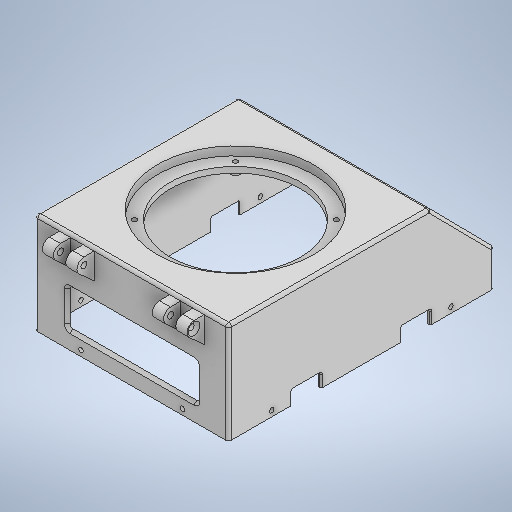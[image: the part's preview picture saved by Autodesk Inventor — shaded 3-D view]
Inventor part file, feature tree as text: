
AUTODESK INVENTOR PART (.ipt)
format: ipt  version: 2025.1 (Build 291241000, 241)  size: 621,056 bytes
history: native  units: mm
features: extrude x16, sketch x16, fillet x5, chamfer x3, other x2
ambient origin geometry x8: Origin, YZ Plane, XZ Plane, XY Plane, X Axis, Y Axis, Z Axis, Center Point
bodies: Body1 (feature_tree)
feature tree (42):
  other  "Sólido1"
  extrude  "Extrusión1"  Depth=70.0mm
  extrude  "Extrusión2"  Depth=184.4mm
  extrude  "Extrusión3"  Depth=45.0mm
  extrude  "Extrusión4"  Depth=45.0mm
  extrude  "Extrusión5"  Depth=9.0mm
  extrude  "Extrusión6"  Depth=2.0mm
  extrude  "Extrusión7"  Depth=2.0mm TaperAngle=0.0deg
  extrude  "Extrusión8"  Depth=90.4mm
  extrude  "Extrusión9"  Depth=3.0mm
  extrude  "Extrusión10"  Depth=9.0mm
  chamfer  "Chaflán2"  Distance=6.0mm
  extrude  "Extrusión11"  Depth=4.0mm
  other  "Cara para el ángulo de desmoldeo1"
  fillet  "Empalme1"  Radius=32.0mm
  fillet  "Empalme2"  Radius=4.0mm
  fillet  "Empalme3"  Radius=3.25mm
  fillet  "Empalme4"  Radius=3.25mm
  fillet  "Empalme5"  Radius=200.0mm
  extrude  "Extrusión12"  Depth=4.0mm
  extrude  "Extrusión13"  Depth=4.0mm
  extrude  "Extrusión14"  Depth=3.25mm
  extrude  "Extrusión15"  Depth=12.0mm
  chamfer  "Chaflán3"  Distance=22.0mm
  extrude  "Extrusión16"  Depth=2.0mm
  chamfer  "Chaflán5"  Distance=2.0mm
  sketch  "Boceto1"  dims[d0=70.0mm d1=140.0mm]
  sketch  "Boceto4"  dims[d3=25.0mm d4=184.4mm]
  sketch  "Boceto5"  dims[d5=72.0mm d6=45.0mm]
  sketch  "Boceto6"  dims[d7=45.0mm d8=45.0mm]
  sketch  "Boceto7"  dims[d9=9.0mm d10=9.0mm]
  sketch  "Boceto8"  dims[d11=130.4mm d12=0.0mm d14=2.0mm]
  sketch  "Boceto9"  dims[d15=2.0mm d16=0.0mm d17=2.0mm d18=0.0mm]
  sketch  "Boceto10"  dims[d19=72.0mm d20=90.4mm]
  sketch  "Boceto11"  dims[d21=3.0mm d22=0.0mm d23=16.3mm]
  sketch  "Boceto12"  dims[d24=8.0mm d25=0.0mm d26=9.0mm d27=6.0mm d28=0.0mm]
  sketch  "Boceto13"  dims[d29=32.0mm d30=4.0mm d31=32.0mm d32=4.0mm d33=3.25mm d34=3.25mm d35=200.0mm d36=0.0mm]
  sketch  "Boceto14"  dims[d37=30.0mm d38=4.0mm]
  sketch  "Boceto15"  dims[d39=30.0mm d40=4.0mm]
  sketch  "Boceto16"  dims[d41=3.25mm d42=3.25mm]
  sketch  "Boceto17"  dims[d43=150.0mm d44=0.0mm d45=12.0mm]
  sketch  "Boceto18"  dims[d47=22.0mm d48=22.0mm d49=25.0mm d50=2.0mm d51=5.0mm d52=0.0mm d53=50.0mm d54=36.7mm d55=68.0mm d56=36.4mm d57=3.25mm d58=3.25mm d59=3.25mm d60=3.25mm d61=10.0mm d62=0.0mm d66=2.0mm d67=2.0mm d68=45.0deg d74=10.0mm d75=0.0mm d79=45.0deg d80=90.0deg d81=3.25mm d82=3.25mm d83=3.25mm d84=3.25mm d117=60.0deg d118=2.0mm d119=2.0mm d120=2.0mm d121=2.0mm d122=2.0mm d123=2.0mm d124=2.0mm d125=2.0mm d126=2.0mm d127=4.0mm d128=0.0mm d129=2.0mm d130=2.0mm d131=2.0mm d132=2.0mm d133=2.0mm d134=0.0mm d135=15.0mm d136=18.0mm d137=7.75mm d138=18.0mm d139=8.5mm d140=7.75mm d141=18.0mm d142=12.0mm d143=0.0mm d144=4.25mm d145=2.75mm d146=7.0mm d148=150.0mm d149=0.0mm d150=2.0mm d151=2.0mm d152=45.0deg d157=20.0mm d158=9.0mm d159=1.0mm d160=38.0mm d161=200.0mm d162=0.0mm d166=1.0mm d167=2.0mm d168=45.0deg d169=90.4mm d171=90.0mm d172=4.5mm d173=2.0mm d174=2.0mm d175=3.25mm d176=3.25mm d177=3.25mm d178=3.25mm d179=3.25mm d180=3.25mm d181=3.25mm d182=3.25mm]
